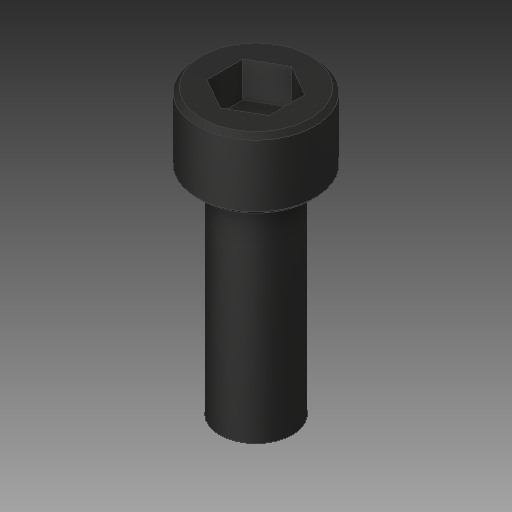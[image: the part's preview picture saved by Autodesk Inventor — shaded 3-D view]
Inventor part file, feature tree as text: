
AUTODESK INVENTOR PART (.ipt)
format: ipt  version: 2017 SP1 (Build 210196100, 196)  size: 103,424 bytes
history: native  units: in
note: dims shown in document units (in); Inventor stores cm internally (conversion verified against a paired STEP export)
features: chamfer x1
ambient origin geometry x8: Origin, YZ Plane, XZ Plane, XY Plane, X Axis, Y Axis, Z Axis, Center Point
bodies: Solid1 (feature_tree)
feature tree (1):
  chamfer  "Chamfer2"  [1 undecoded]
note: 1 required parameter value undecoded (feature->parameter linkage not recoverable at this tier; creation-order binding heuristic only, values carry confidence <= 0.55)
